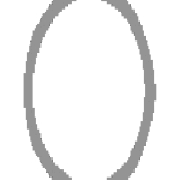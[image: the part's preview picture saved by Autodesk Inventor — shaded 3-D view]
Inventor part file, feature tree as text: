
AUTODESK INVENTOR PART (.ipt)
format: ipt  version: 2021 (Build 250183000, 183)  size: 145,920 bytes
history: native  units: in
note: dims shown in document units (in); Inventor stores cm internally (conversion verified against a paired STEP export)
features: plane x7, sketch x5, other x4, extrude x2, boolean_combine x2
ambient origin geometry x8: Origin, YZ Plane, XZ Plane, XY Plane, X Axis, Y Axis, Z Axis, Center Point
bodies: Solid1 (feature_tree), Body (feature_tree), Solid2 (feature_tree), Solid3 (feature_tree)
feature tree (20):
  other  "Driven Length"
  other  "Frame Generator"
  other  "Start Plane"
  other  "End Plane"
  plane  "Work Plane4"
  plane  "Work Plane5"
  plane  "Work Plane6"
  extrude  "Extrusion3"  Depth=0.065in
  boolean_combine  "Combine1"
  plane  "Work Plane7"
  plane  "Work Plane8"
  plane  "Work Plane9"
  extrude  "Extrusion4"  TaperAngle=0.0deg  [1 undecoded]
  boolean_combine  "Combine2"
  sketch  "Sketch"  dims[d8=90.0deg d9=3.0in d10=0.12in d11=0.0in d12=0.12in d13=0.0in]
  sketch  "Sketch2"  dims[d0=1.0in d1=0.065in]
  plane  "Work Plane3"
  sketch  "Sketch3"  dims[d2=3.0in d4=-0.0in]
  sketch  "Sketch4"  dims[d5=3.0in]
  sketch  "Sketch5"  dims[d6=0.12in d7=0.0in]
note: 1 required parameter value undecoded (feature->parameter linkage not recoverable at this tier; creation-order binding heuristic only, values carry confidence <= 0.55)
